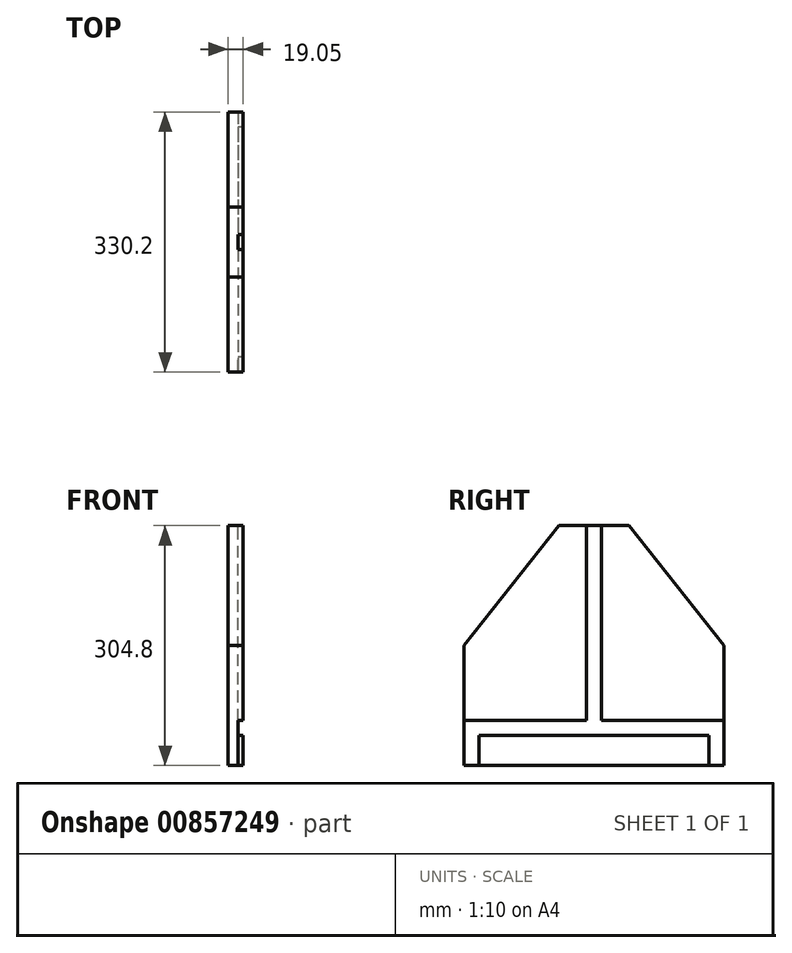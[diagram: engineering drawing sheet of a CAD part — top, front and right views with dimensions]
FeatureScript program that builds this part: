
annotation { "Feature Type Name" : "Feature", "Feature Type Description" : "" }
export const myFeature = defineFeature(function(context is Context, id is Id, definition is map)
    precondition{}
    {
        {
            var Q0;
            Q0=qCreatedBy(makeId("Right.planeOp"),FACE);
            var sketch = newSketch(context, id + "F0", { "sketchPlane" : qUnion([Q0])});
            skLineSegment(sketch, "E0.top", {"start": v(-120.65, -125.13) * mm, "end": v(209.55, -125.13) * mm});
            skPoint(sketch, "E1.middle", {"position": v(44.45, 179.67) * mm});
            skLineSegment(sketch, "E2", {"start": v(-120.65, 27.27) * mm, "end": v(0, 179.67) * mm});
            skLineSegment(sketch, "E3", {"start": v(0, 179.67) * mm, "end": v(88.9, 179.67) * mm});
            skLineSegment(sketch, "E4", {"start": v(88.9, 179.67) * mm, "end": v(209.55, 27.27) * mm});
            skLineSegment(sketch, "E5", {"start": v(209.55, 27.27) * mm, "end": v(209.55, -125.13) * mm});
            skLineSegment(sketch, "E6", {"start": v(-120.65, -125.13) * mm, "end": v(-120.65, 27.27) * mm});
            skSolve(sketch);
        }
        {
            var Q0;
            {var subQ1=sQuery(id+"F0.wireOp",EDGE,"EUrnNOh8-34OH-eLoF-MlDC-UtxF3qT7OUsE.top");Q0=makeQuery(id+"F0.imprint","IMPRINT",FACE,{"disambiguationData":[TD([[makeQuery(id+"F0.imprint","IMPRINT",EDGE,{"derivedFrom":subQ1}),1.0]])]});}
            var Q1;
            Q1=makeQuery(id+"F0.imprint","IMPRINT",FACE,{"disambiguationData":[TD([[makeQuery(id+"F0.imprint","IMPRINT",EDGE,{"derivedFrom":sQuery(id+"F0.wireOp",EDGE,"E0.top")}),1.0]])]});
            extrude(context, id + "F1", {"entities" : qUnion([Q0, Q1]), "depth" : 19.05 * mm, "offsetDistance" : 25.4 * mm});
        }
        {
            var Q0;
            Q0=makeQuery(id+"F1.opExtrude","SWEPT_FACE",FACE,{"disambiguationData":[OSD([sQuery(id+"F0.wireOp",EDGE,"E6")])]});
            var sketch = newSketch(context, id + "F2", { "sketchPlane" : qUnion([Q0])});
            skLineSegment(sketch, "E7.bottom", {"start": v(19.05, -87.03) * mm, "end": v(12.7, -87.03) * mm});
            skLineSegment(sketch, "E7.top", {"start": v(19.05, -67.98) * mm, "end": v(12.7, -67.98) * mm});
            skLineSegment(sketch, "E7.left", {"start": v(19.05, -87.03) * mm, "end": v(19.05, -67.98) * mm});
            skLineSegment(sketch, "E7.right", {"start": v(12.7, -87.03) * mm, "end": v(12.7, -67.98) * mm});
            skSolve(sketch);
        }
        {
            var Q0;
            Q0=makeQuery(id+"F2.imprint","IMPRINT",FACE,{"disambiguationData":[TD([[makeQuery(id+"F2.imprint","IMPRINT",EDGE,{"derivedFrom":sQuery(id+"F2.wireOp",EDGE,"E7.bottom")}),-1.0]])]});
            extrude(context, id + "F3", {"entities" : qUnion([Q0]), "operationType" : NewBodyOperationType.REMOVE, "oppositeDirection" : true, "depth" : 330.2 * mm, "offsetDistance" : 25.4 * mm});
        }
        {
            var Q0;
            Q0=makeQuery(id+"F1.opExtrude","SWEPT_FACE",FACE,{"disambiguationData":[OSD([sQuery(id+"F0.wireOp",EDGE,"E0.top")])]});
            var sketch = newSketch(context, id + "F4", { "sketchPlane" : qUnion([Q0])});
            skLineSegment(sketch, "E8.bottom", {"start": v(19.05, 120.65) * mm, "end": v(12.7, 120.65) * mm});
            skLineSegment(sketch, "E8.top", {"start": v(19.05, 101.6) * mm, "end": v(12.7, 101.6) * mm});
            skLineSegment(sketch, "E8.left", {"start": v(19.05, 120.65) * mm, "end": v(19.05, 101.6) * mm});
            skLineSegment(sketch, "E8.right", {"start": v(12.7, 120.65) * mm, "end": v(12.7, 101.6) * mm});
            skLineSegment(sketch, "E9.bottom", {"start": v(19.05, -209.55) * mm, "end": v(12.7, -209.55) * mm});
            skLineSegment(sketch, "E9.top", {"start": v(19.05, -190.5) * mm, "end": v(12.7, -190.5) * mm});
            skLineSegment(sketch, "E9.left", {"start": v(19.05, -209.55) * mm, "end": v(19.05, -190.5) * mm});
            skLineSegment(sketch, "E9.right", {"start": v(12.7, -209.55) * mm, "end": v(12.7, -190.5) * mm});
            skSolve(sketch);
        }
        {
            var Q0;
            Q0=makeQuery(id+"F4.imprint","IMPRINT",FACE,{"disambiguationData":[TD([[makeQuery(id+"F4.imprint","IMPRINT",EDGE,{"derivedFrom":sQuery(id+"F4.wireOp",EDGE,"E8.bottom")}),1.0]])]});
            var Q1;
            Q1=makeQuery(id+"F4.imprint","IMPRINT",FACE,{"disambiguationData":[TD([[makeQuery(id+"F4.imprint","IMPRINT",EDGE,{"derivedFrom":sQuery(id+"F4.wireOp",EDGE,"E9.bottom")}),-1.0]])]});
            extrude(context, id + "F5", {"entities" : qUnion([Q0, Q1]), "operationType" : NewBodyOperationType.REMOVE, "oppositeDirection" : true, "depth" : 38.1 * mm, "offsetDistance" : 25.4 * mm});
        }
        {
            var Q0;
            Q0=makeQuery(id+"F1.opExtrude","SWEPT_FACE",FACE,{"disambiguationData":[OSD([sQuery(id+"F0.wireOp",EDGE,"E3")])]});
            var sketch = newSketch(context, id + "F6", { "sketchPlane" : qUnion([Q0])});
            skLineSegment(sketch, "E10.bottom", {"start": v(12.7, 53.98) * mm, "end": v(25.4, 53.98) * mm});
            skLineSegment(sketch, "E10.top", {"start": v(12.7, 34.93) * mm, "end": v(25.4, 34.93) * mm});
            skLineSegment(sketch, "E10.left", {"start": v(12.7, 53.98) * mm, "end": v(12.7, 34.93) * mm});
            skLineSegment(sketch, "E10.right", {"start": v(25.4, 53.98) * mm, "end": v(25.4, 34.93) * mm});
            skPoint(sketch, "E10.middle", {"position": v(19.05, 44.45) * mm});
            skSolve(sketch);
        }
        {
            var Q0;
            {var subQ0=sQuery(id+"F6.wireOp",EDGE,"E10.left");Q0=makeQuery(id+"F6.imprint","IMPRINT",FACE,{"disambiguationData":[TD([[makeQuery(id+"F6.imprint","IMPRINT",EDGE,{"derivedFrom":subQ0}),1.0]])]});}
            extrude(context, id + "F7", {"entities" : qUnion([Q0]), "operationType" : NewBodyOperationType.REMOVE, "oppositeDirection" : true, "depth" : 247.65 * mm, "offsetDistance" : 25.4 * mm});
        }
    });
